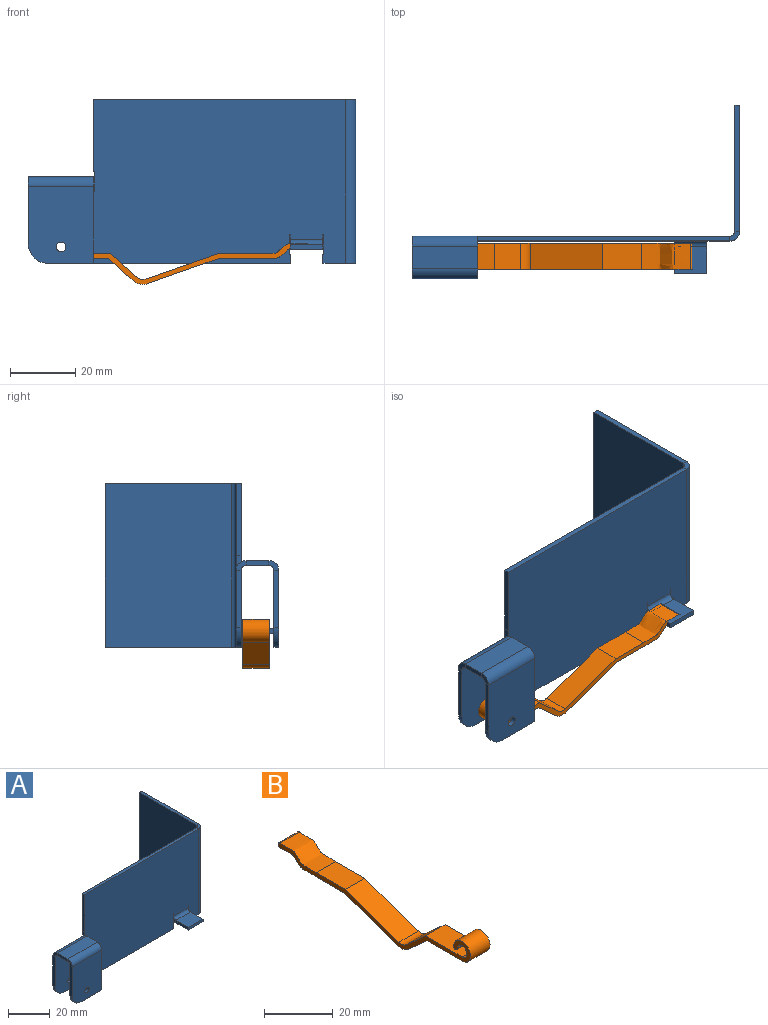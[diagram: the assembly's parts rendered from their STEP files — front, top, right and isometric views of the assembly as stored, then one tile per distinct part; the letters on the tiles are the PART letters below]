
ASSEMBLY  parts=2 mates=1
PART A: 66 faces, bbox 100x53x50 mm
  f0: plane 1.5x1.5mm, normal (1,0,0), area 2.2mm2, adj f1,f4,f5,f40
  f1: cylinder r=0.07mm len=1.5mm, axis (0,0,1), area 0.2mm2, adj f0,f2,f4,f5
  f2: plane 5.43x1.5mm, normal (1,0,0), area 8.1mm2, adj f1,f4,f5,f6
  f3: plane 7x1.5mm, normal (-1,0,0), area 10.5mm2, adj f4,f5,f7,f41
  f4: plane 20x7mm, normal (0,0,-1), area 139.9mm2, adj f0,f1,f2,f3,f8,f42
  f5: plane 20x7mm, normal (0,0,1), area 139.9mm2, adj f0,f1,f2,f3,f9,f43
  f6: plane 3x3mm, normal (1,0,0), area 5.3mm2, adj f2,f8,f9,f14
  f7: plane 3x3mm, normal (-1,0,0), area 5.3mm2, adj f3,f8,f9,f16
  f8: cylinder r=1.5mm len=20mm, axis (-1,0,0), area 47.1mm2, adj f4,f6,f7,f13
  f9: cylinder r=3mm len=20mm, axis (-1,0,0), area 94.2mm2, adj f5,f6,f7,f15
  f10: cylinder r=6mm len=6mm, axis (0,-1,0), area 14.1mm2, adj f11,f13,f15,f16
  f11: plane 14x1.5mm, normal (0,0,-1), area 21mm2, adj f10,f13,f14,f15
  f12: cylinder r=1.5mm len=3mm, axis (0,-1,0), area 14.1mm2, adj f13,f15
  f13: plane 23.5x20mm, normal (0,1,0), area 455.2mm2, adj f8,f10,f11,f12,f14,f16
  f14: plane 23.5x1.5mm, normal (1,0,0), area 35.2mm2, adj f6,f11,f13,f15
  f15: plane 23.5x20mm, normal (0,-1,0), area 455.2mm2, adj f9,f10,f11,f12,f14,f16
  f16: plane 17.5x1.5mm, normal (-1,0,0), area 26.2mm2, adj f7,f10,f13,f15
  f17: cylinder r=1.5mm len=3mm, axis (0,-1,0), area 14.1mm2, adj f36,f38
  f18: plane 1.5x0.15mm, normal (0,0,-1), area 0.2mm2, adj f19,f35,f36,f38
  f19: plane 6x1.5mm, normal (1,0,0), area 9mm2, adj f18,f20,f36,f38
  f20: plane 1.5x0.08mm, normal (0,0,1), area 0.1mm2, adj f19,f21,f36,f38
  f21: plane 2.75x1.5mm, normal (1,0,0), area 4.1mm2, adj f20,f22,f36,f38
  f22: plane 74x1.5mm, normal (0,0,-1), area 111mm2, adj f21,f23,f36,f38
  f23: cylinder r=6mm len=6mm, axis (0,-1,0), area 14.1mm2, adj f22,f36,f37,f38
  f24: plane 1.5x0.15mm, normal (0,0,1), area 0.2mm2, adj f25,f36,f38,f39
  f25: plane 6x1.5mm, normal (-1,0,0), area 9mm2, adj f24,f26,f36,f38
  f26: plane 1.5x0.08mm, normal (0,0,-1), area 0.1mm2, adj f25,f27,f36,f38
  f27: plane 22x1.5mm, normal (-1,0,0), area 33mm2, adj f26,f28,f36,f38
  f28: plane 77x1.5mm, normal (0,0,1), area 115.5mm2, adj f27,f36,f38,f57
  f29: plane 7x1.5mm, normal (0,0,-1), area 10.5mm2, adj f30,f36,f38,f58
  f30: plane 2.75x1.5mm, normal (-1,0,0), area 4.1mm2, adj f29,f31,f36,f38
  f31: plane 1.5x0.08mm, normal (0,0,1), area 0.1mm2, adj f30,f32,f36,f38
  f32: plane 6x1.5mm, normal (-1,0,0), area 9mm2, adj f31,f33,f36,f38
  f33: plane 1.5x0.15mm, normal (0,0,-1), area 0.2mm2, adj f32,f34,f36,f38
  f34: plane 1.5x1.5mm, normal (1,0,0), area 2.3mm2, adj f33,f36,f38,f45
  f35: plane 1.5x1.5mm, normal (-1,0,0), area 2.3mm2, adj f18,f36,f38,f44
  f36: plane 97x50mm, normal (0,-1,0), area 4231mm2, adj f17,f18,f19,f20,f21,f22,f23,f24
  f37: plane 17.5x1.5mm, normal (-1,0,0), area 26.3mm2, adj f23,f36,f38,f41
  f38: plane 97x50mm, normal (0,1,0), area 4231mm2, adj f17,f18,f19,f20,f21,f22,f23,f24
  f39: plane 1.5x1.5mm, normal (1,0,0), area 2.3mm2, adj f24,f36,f38,f40
  f40: plane 3x3mm, normal (1,0,0), area 5.3mm2, adj f0,f39,f42,f43
  f41: plane 3x3mm, normal (-1,0,0), area 5.3mm2, adj f3,f37,f42,f43
  f42: cylinder r=1.5mm len=19.93mm, axis (-1,0,0), area 46.9mm2, adj f4,f36,f40,f41
  f43: cylinder r=3mm len=19.93mm, axis (-1,0,0), area 93.9mm2, adj f5,f38,f40,f41
  f44: plane 3x3mm, normal (-1,0,0), area 5.3mm2, adj f35,f46,f47,f54
  f45: plane 3x3mm, normal (1,0,0), area 5.3mm2, adj f34,f46,f47,f56
  f46: cylinder r=1.5mm len=9.85mm, axis (1,0,0), area 23.2mm2, adj f36,f44,f45,f53
  f47: cylinder r=3mm len=9.85mm, axis (1,0,0), area 46.4mm2, adj f38,f44,f45,f55
  f48: cylinder r=0.07mm len=1.5mm, axis (0,0,-1), area 0.2mm2, adj f49,f53,f55,f56
  f49: plane 6.93x1.5mm, normal (1,0,0), area 10.4mm2, adj f48,f50,f53,f55
  f50: plane 10x1.5mm, normal (0,-1,0), area 15mm2, adj f49,f51,f53,f55
  f51: plane 6.93x1.5mm, normal (-1,0,0), area 10.4mm2, adj f50,f52,f53,f55
  f52: cylinder r=0.07mm len=1.5mm, axis (0,0,-1), area 0.2mm2, adj f51,f53,f54,f55
  f53: plane 10x8.5mm, normal (0,0,1), area 84.8mm2, adj f46,f48,f49,f50,f51,f52,f54,f56
  f54: plane 1.5x1.5mm, normal (-1,0,0), area 2.3mm2, adj f44,f52,f53,f55
  f55: plane 10x8.5mm, normal (0,0,-1), area 84.8mm2, adj f47,f48,f49,f50,f51,f52,f54,f56
  f56: plane 1.5x1.5mm, normal (1,0,0), area 2.3mm2, adj f45,f48,f53,f55
  f57: plane 3x3mm, normal (0,0,1), area 5.3mm2, adj f28,f59,f60,f65
  f58: plane 3x3mm, normal (0,0,-1), area 5.3mm2, adj f29,f59,f60,f63
  f59: cylinder r=3mm len=50mm, axis (0,0,1), area 235.6mm2, adj f36,f57,f58,f62
  f60: cylinder r=1.5mm len=50mm, axis (0,0,1), area 117.8mm2, adj f38,f57,f58,f64
  f61: plane 50x1.5mm, normal (0,1,0), area 75mm2, adj f62,f63,f64,f65
  f62: plane 50x38.5mm, normal (1,0,0), area 1925mm2, adj f59,f61,f63,f65
  f63: plane 38.5x1.5mm, normal (0,0,-1), area 57.7mm2, adj f58,f61,f62,f64
  f64: plane 50x38.5mm, normal (-1,0,0), area 1925mm2, adj f60,f61,f63,f65
  f65: plane 38.5x1.5mm, normal (0,0,1), area 57.7mm2, adj f57,f61,f62,f64
PART B: 18 faces, bbox 8x79.3x14.9 mm
  f0: plane 11.74x8mm, normal (0,0,-1), area 93.9mm2, adj f1,f15,f16,f17
  f1: extruded ~15x8mm, area 128.1mm2, adj f0,f2,f16,f17
  f2: cylinder r=0.75mm len=8mm, axis (-1,0,0), area 18.8mm2, adj f1,f3,f16,f17
  f3: extruded ~15x8mm, area 128.2mm2, adj f2,f4,f16,f17
  f4: plane 12x8mm, normal (0,0,1), area 96mm2, adj f3,f5,f16,f17
  f5: plane 22x8mm, normal (0,-0.33,0.94), area 186.7mm2, adj f4,f6,f16,f17
  f6: cylinder r=3mm len=8mm, axis (-1,0,0), area 25.7mm2, adj f5,f7,f16,f17
  f7: plane 8x8mm, normal (0,0.67,0.74), area 86mm2, adj f6,f8,f16,f17
  f8: plane 15x8mm, normal (0,0,1), area 120mm2, adj f7,f9,f16,f17
  f9: cylinder r=2mm len=8mm, axis (-1,0,0), area 75.4mm2, adj f8,f10,f16,f17
  f10: cylinder r=0.75mm len=8mm, axis (-1,0,0), area 18.8mm2, adj f9,f11,f16,f17
  f11: cylinder r=3.5mm len=8mm, axis (-1,0,0), area 131.9mm2, adj f10,f12,f16,f17
  f12: plane 14.43x8mm, normal (0,0,-1), area 115.4mm2, adj f11,f13,f16,f17
  f13: plane 8x7.57mm, normal (0,-0.67,-0.74), area 81.4mm2, adj f12,f14,f16,f17
  f14: cylinder r=4.5mm len=8mm, axis (-1,0,0), area 38.6mm2, adj f13,f15,f16,f17
  f15: plane 21.76x8mm, normal (0,0.33,-0.94), area 184.6mm2, adj f0,f14,f16,f17
  f16: plane 79.25x14.95mm, normal (1,0,0), area 141.7mm2, adj f0,f1,f2,f3,f4,f5,f6,f7
  f17: plane 79.25x14.95mm, normal (-1,0,0), area 141.7mm2, adj f0,f1,f2,f3,f4,f5,f6,f7
PLACE A t=(-13.86,0,22.73)mm
PLACE B rot(axis=(0,0,-1),90deg) t=(-103.86,-2.06,25.73)mm
MATE cylindrical B.f9 <-> A.f12  axis (0,-1,0) through (-103.86,-10.06,27.73)mm
